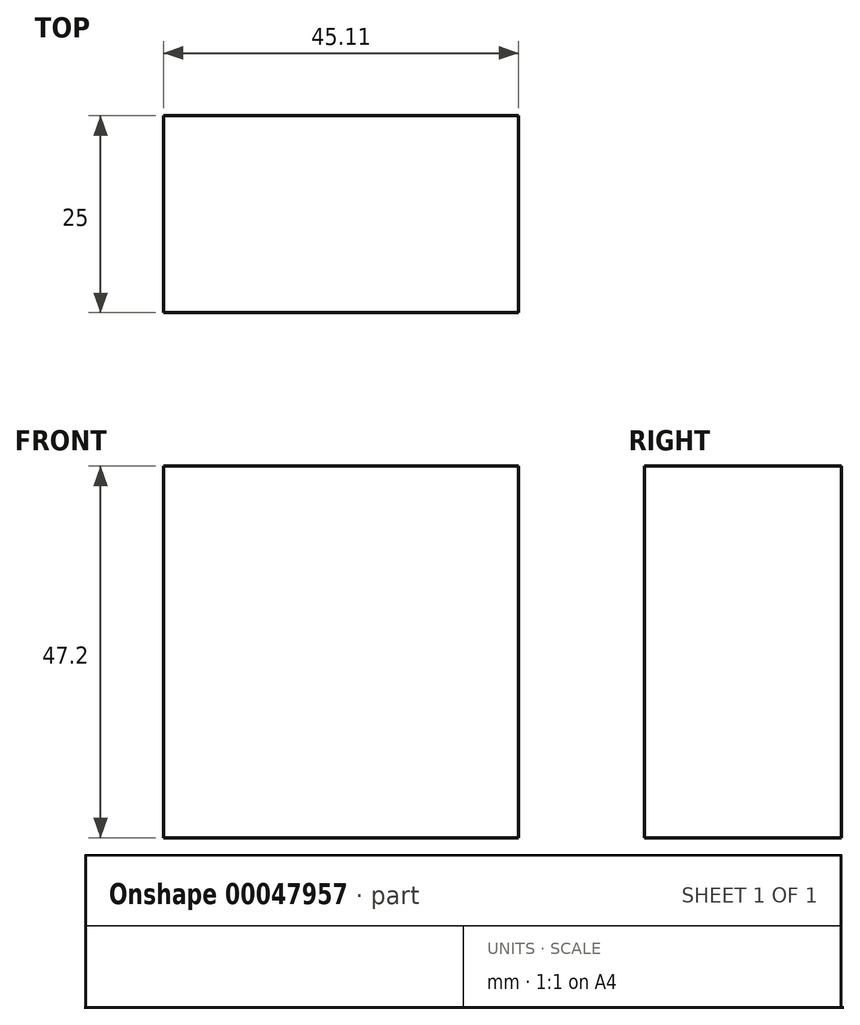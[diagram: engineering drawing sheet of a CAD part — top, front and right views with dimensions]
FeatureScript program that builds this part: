
annotation { "Feature Type Name" : "Feature", "Feature Type Description" : "" }
export const myFeature = defineFeature(function(context is Context, id is Id, definition is map)
    precondition{}
    {
        {
            var Q0;
            Q0=qCreatedBy(makeId("Front.planeOp"),FACE);
            var sketch = newSketch(context, id + "F0", { "sketchPlane" : qUnion([Q0])});
            skLineSegment(sketch, "E0.bottom", {"start": v(0, 0) * mm, "end": v(45.11, 0) * mm});
            skLineSegment(sketch, "E0.top", {"start": v(0, 47.2) * mm, "end": v(45.11, 47.2) * mm});
            skLineSegment(sketch, "E0.left", {"start": v(0, 0) * mm, "end": v(0, 47.2) * mm});
            skLineSegment(sketch, "E0.right", {"start": v(45.11, 0) * mm, "end": v(45.11, 47.2) * mm});
            skSolve(sketch);
        }
        {
            var Q0;
            Q0=makeQuery(id+"F0.imprint","IMPRINT",FACE,{"disambiguationData":[TD([[makeQuery(id+"F0.imprint","IMPRINT",EDGE,{"derivedFrom":sQuery(id+"F0.wireOp",EDGE,"E0.bottom")}),1.0]])]});
            var Q1;
            Q1=makeQuery(id+"F0.imprint","IMPRINT",FACE,{"disambiguationData":[TD([[makeQuery(id+"F0.imprint","IMPRINT",EDGE,{"derivedFrom":sQuery(id+"F0.wireOp",EDGE,"E0.bottom")}),1.0]])]});
            extrude(context, id + "F1", {"entities" : qUnion([Q0, Q1]), "depth" : 25 * mm});
        }
    });
